# Revit family: HerzCon-Direktanschluss für FanCoils 120mm
name_source: partatom
category: Rohrzubehör
revit_build: Autodesk Revit 2018 (Build: 20190510_1515(x64)
units: mm (PartAtom-declared; Revit-internal decimal feet)

## family parameters
Arbeitsebenenbasiert = Nein
Beim Laden mit Abzugskörper schneiden = Nein
Bemaßung runder Anschluss = Durchmesser verwenden
Gemeinsam genutzt = Nein
Immer vertikal = Ja
OmniClass-Nummer = 23.65.55.14
OmniClass-Titel = Valves for Liquid Services
Teiletyp = Unterbricht

## types (1)
- DN32
    Anwendungen = Die HerzCON wurden entwickelt, um eine einfache Verbindung zu Gebläsekonvektoren oder anderen Anschlusseinheiten herzustellen.
Ein HerzCON ist eine Einheit, bestehend aus einem druckunabhängigen Kombiventil-Volumenstromregler (4006), Herz-Schmutzfänger, Herz-Entleerungshahn (2512) und zwei Herz-Multifunktionskugelhähnen.
Das Ein-/ Aus Schalten sowie Modulieren ist über einen 0-10 V Stellantrieb möglich und kann bei Bedarf in eine GLT integriert werden.
Die Einheit optimiert die Energieeffizienz des Systems, da es eine druckunabhängige Regelung ist, die den vollen Regelbereich unabhängig von Druckschwankungen gewährleistet, während gleichzeitig ein konstanter Durchfluss sichergestellt wird.
Mit der HerzCON können auch Spül- und Absperrvorgänge durchgeführt werden.
Eine Einheit kann für Heizen und Kühlen verwendet werden.
Es gibt daher keinen Produktunterschied zwischen Heizen und Kühlen.
Der am Sieb angebrachte Ablasshahn ermöglicht ein Spülen, ohne dass der Siebkorb entfernt werden muss.
Außerdem kann der Siebkorb vor Ort gereinigt werden.
    D01 = 15 mm  [stored 0.0492126 ft]
    D02 = 33 mm  [stored 0.108268 ft]
    D03 = 24.5 mm  [stored 0.0803806 ft]
    D04 = 20 mm  [stored 0.0656168 ft]
    D05 = 54.5 mm  [stored 0.178806 ft]
    D06 = 45 mm  [stored 0.147638 ft]
    D07 = 39 mm  [stored 0.127953 ft]
    D08 = 18.4 mm  [stored 0.0603675 ft]
    D09 = 13 mm
    D10 = 21.4 mm  [stored 0.07021 ft]
    Gehäuse = entzinkungsbeständiges Messing
    H01 = 34 mm
    Hersteller = HERZ Armaturen Ges.m.b.H.
    Hub = 4 mm
    KD01 = 25 mm  [stored 0.082021 ft]
    KD02 = 20 mm  [stored 0.0656168 ft]
    KD03 = 20 mm  [stored 0.0656168 ft]
    KD04 = 13.9 mm  [stored 0.0456037 ft]
    KD05 = 12.5 mm  [stored 0.0410105 ft]
    KD06 = 15 mm  [stored 0.0492126 ft]
    KD07 = 23.3 mm
    KD08 = 24.5 mm  [stored 0.0803806 ft]
    KD09 = 11.25 mm  [stored 0.0369094 ft]
    KH01 = 33.5 mm  [stored 0.109908 ft]
    KH02 = 58.5 mm  [stored 0.191929 ft]
    KH03 = 66 mm  [stored 0.216535 ft]
    KL01 = 114 mm  [stored 0.374016 ft]
    KL02 = 16 mm  [stored 0.0524934 ft]
    KL03 = 57 mm  [stored 0.187008 ft]
    KL04 = 12 mm  [stored 0.0393701 ft]
    KL05 = 15.4 mm
    KL06 = 48.9 mm  [stored 0.160433 ft]
    KL07 = 21.8 mm  [stored 0.0715223 ft]
    KL08 = 70.7 mm  [stored 0.231955 ft]
    KL09 = 4.7 mm  [stored 0.0154199 ft]
    KR01 = 35 mm  [stored 0.114829 ft]
    KR02 = 18.25 mm  [stored 0.0598753 ft]
    L01 = 15 mm  [stored 0.0492126 ft]
    L02 = 6.1 mm  [stored 0.0200131 ft]
    L03 = 22.4 mm  [stored 0.0734908 ft]
    L04 = 55 mm  [stored 0.180446 ft]
    L05 = 26.5 mm  [stored 0.0869423 ft]
    L06 = 17 mm
    L07 = 19.25 mm  [stored 0.0631562 ft]
    L08 = 14.75 mm
    L09 = 20 mm  [stored 0.0656168 ft]
    L10 = 29.3 mm  [stored 0.0961286 ft]
    L11 = 16 mm  [stored 0.0524934 ft]
    Max. Betriebsdruck = 2500000.0 Pa
    Max. Betriebstemperatur = 130 °C
    Max. Differenzdruck = 400000.0 Pa
    Medium = Heizungswasser gemäß ÖNORM H5195 oder VDI-Standard 2035.
Die Verwendung von Ethylen- oder Propylenglykol-Gemischen in einem Verhältnis von 25-50 Vol.- % ist erlaubt.
    Membrane und O-Ringe = EPDM
    Min. Betriebstemperatur = -20 °C
    SCRNCODE = 05;04;04
    SCRNSEQ = ARM;TYP_ARM="DURR";02
    URL = www.herz-armaturen.at
    kvs-Wert (Bypass Funktion) = 14.2
    kvs-Wert (normale Funktion) = 4.57

note: [stored X ft] marks values corroborated as IEEE doubles in the binary element streams (Revit-internal decimal feet)
